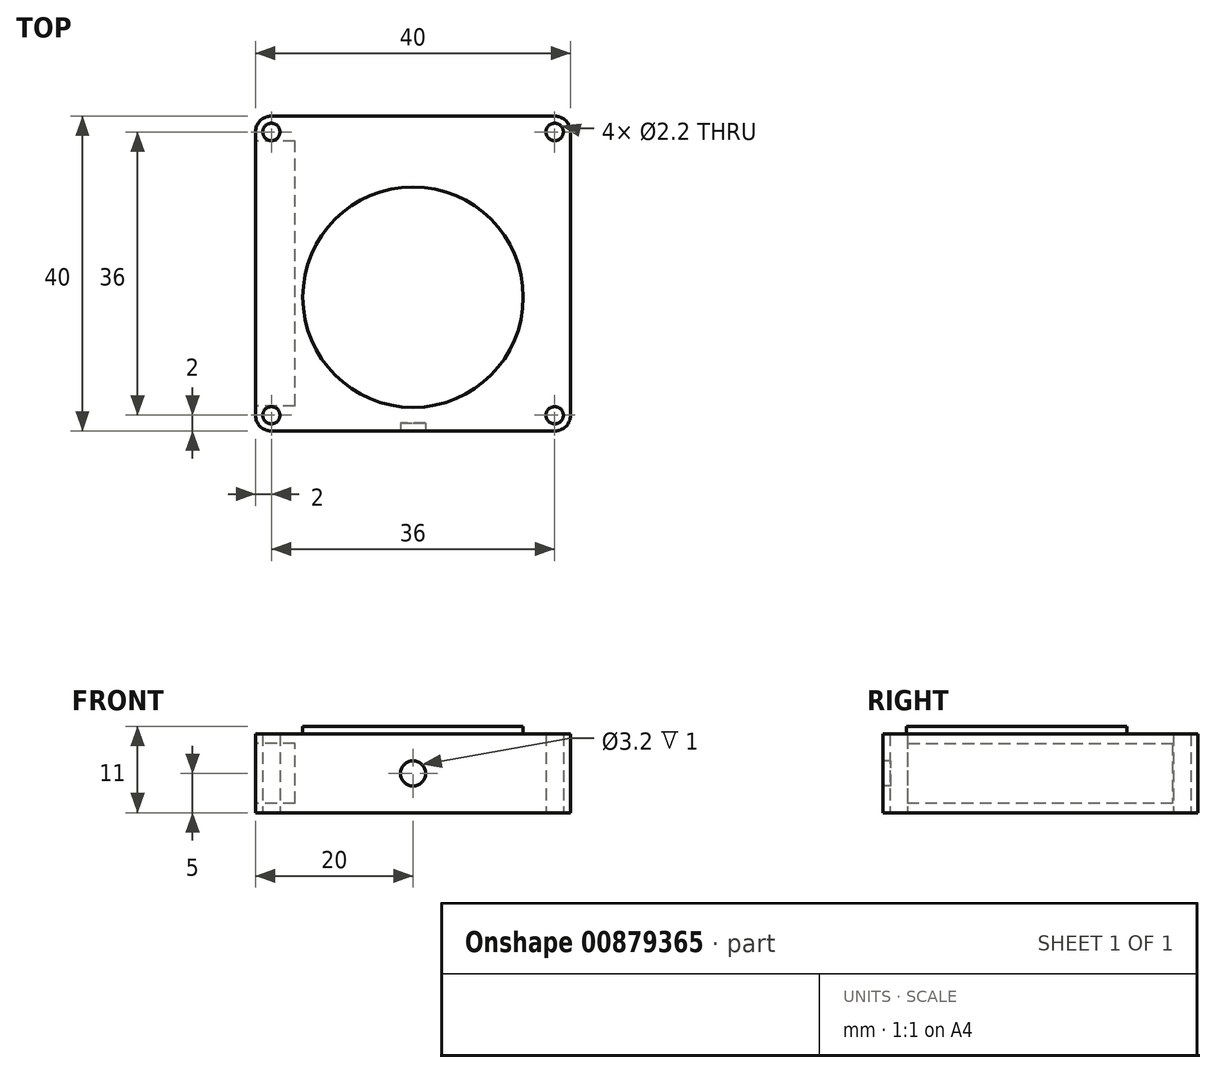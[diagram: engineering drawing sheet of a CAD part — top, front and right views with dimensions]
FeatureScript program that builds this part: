
annotation { "Feature Type Name" : "Feature", "Feature Type Description" : "" }
export const myFeature = defineFeature(function(context is Context, id is Id, definition is map)
    precondition{}
    {
        {
            var Q0;
            Q0=qCreatedBy(makeId("Top.planeOp"),FACE);
            var sketch = newSketch(context, id + "F0", { "sketchPlane" : qUnion([Q0])});
            skLineSegment(sketch, "E0.bottom", {"start": v(20, -20) * mm, "end": v(-20, -20) * mm});
            skLineSegment(sketch, "E0.top", {"start": v(20, 20) * mm, "end": v(-20, 20) * mm});
            skLineSegment(sketch, "E0.left", {"start": v(20, -20) * mm, "end": v(20, 20) * mm});
            skLineSegment(sketch, "E0.right", {"start": v(-20, -20) * mm, "end": v(-20, 20) * mm});
            skPoint(sketch, "E0.middle", {"position": v(0, 0) * mm});
            skPoint(sketch, "E1", {"position": v(-18, 18) * mm});
            skPoint(sketch, "E2", {"position": v(-18, -18) * mm});
            skPoint(sketch, "E3", {"position": v(18, 18) * mm});
            skPoint(sketch, "E4", {"position": v(18, -18) * mm});
            skSolve(sketch);
        }
        {
            var Q0;
            Q0=makeQuery(id+"F0.imprint","IMPRINT",FACE,{"disambiguationData":[TD([[makeQuery(id+"F0.imprint","IMPRINT",EDGE,{"derivedFrom":sQuery(id+"F0.wireOp",EDGE,"E0.bottom")}),-1.0]])]});
            extrude(context, id + "F1", {"entities" : qUnion([Q0]), "depth" : 10 * mm, "offsetDistance" : 25 * mm});
        }
        {
            var Q0;
            Q0=sQuery(id+"F0.wireOp",VERTEX,"E2");
            var Q1;
            Q1=sQuery(id+"F0.wireOp",VERTEX,"E1");
            var Q2;
            Q2=sQuery(id+"F0.wireOp",VERTEX,"E3");
            var Q3;
            Q3=sQuery(id+"F0.wireOp",VERTEX,"E4");
            var Q4;
            Q4=makeQuery(id+"F1.opExtrude","SWEPT_BODY",BODY,{"disambiguationData":[OSD([sQuery(id+"F0.wireOp",EDGE,"E0.bottom"),sQuery(id+"F0.wireOp",EDGE,"E0.top"),sQuery(id+"F0.wireOp",EDGE,"E0.left"),sQuery(id+"F0.wireOp",EDGE,"E0.right")])]});
            hole(context, id + "F2", {"style" : HoleStyle.SIMPLE, "endStyle" : HoleEndStyle.BLIND, "oppositeDirection" : true, "holeDiameter" : 2.2 * mm, "majorDiameter" : 5 * mm, "holeDepth" : 40 * mm, "isTappedThrough" : true, "tappedDepth" : 12 * mm, "tapClearance" : 3, "locations" : qUnion([Q0, Q1, Q2, Q3]), "scope" : qUnion([Q4])});
        }
        {
            var Q0;
            Q0=makeQuery(id+"F1.opExtrude","SWEPT_EDGE",EDGE,{"disambiguationData":[OSD([sQuery(id+"F0.wireOp",EDGE,"E0.bottom"),sQuery(id+"F0.wireOp",EDGE,"E0.right")])]});
            var Q1;
            Q1=makeQuery(id+"F1.opExtrude","SWEPT_EDGE",EDGE,{"disambiguationData":[OSD([sQuery(id+"F0.wireOp",EDGE,"E0.top"),sQuery(id+"F0.wireOp",EDGE,"E0.right")])]});
            var Q2;
            Q2=makeQuery(id+"F1.opExtrude","SWEPT_EDGE",EDGE,{"disambiguationData":[OSD([sQuery(id+"F0.wireOp",EDGE,"E0.bottom"),sQuery(id+"F0.wireOp",EDGE,"E0.left")])]});
            var Q3;
            Q3=makeQuery(id+"F1.opExtrude","SWEPT_EDGE",EDGE,{"disambiguationData":[OSD([sQuery(id+"F0.wireOp",EDGE,"E0.top"),sQuery(id+"F0.wireOp",EDGE,"E0.left")])]});
            fillet(context, id + "F3", {"entities" : qUnion([Q0, Q1, Q2, Q3]), "tangentPropagation" : true, "radius" : 2 * mm, "defaultsChanged" : false, "vertexSettings" : [], "allowEdgeOverflow" : false});
        }
        {
            var Q0;
            Q0=makeQuery(id+"F1.opExtrude","CAP_FACE",FACE,{"disambiguationData":[OSD([sQuery(id+"F0.wireOp",EDGE,"E0.bottom"),sQuery(id+"F0.wireOp",EDGE,"E0.top"),sQuery(id+"F0.wireOp",EDGE,"E0.left"),sQuery(id+"F0.wireOp",EDGE,"E0.right")])],"isStart":false});
            var sketch = newSketch(context, id + "F4", { "sketchPlane" : qUnion([Q0])});
            skCircle(sketch, "E5", {"center": v(0, -3) * mm, "radius": 14 * mm});
            skSolve(sketch);
        }
        {
            var Q0;
            Q0=makeQuery(id+"F4.imprint","IMPRINT",FACE,{"disambiguationData":[TD([[makeQuery(id+"F4.imprint","IMPRINT",EDGE,{"derivedFrom":sQuery(id+"F4.wireOp",EDGE,"E5")}),1.0]])]});
            extrude(context, id + "F5", {"entities" : qUnion([Q0]), "operationType" : NewBodyOperationType.ADD, "depth" : 1 * mm, "offsetDistance" : 25 * mm});
        }
        {
            var Q0;
            Q0=makeQuery(id+"F1.opExtrude","SWEPT_FACE",FACE,{"disambiguationData":[OSD([sQuery(id+"F0.wireOp",EDGE,"E0.right")])]});
            var sketch = newSketch(context, id + "F6", { "sketchPlane" : qUnion([Q0])});
            skLineSegment(sketch, "E6.0", {"start": v(16.8, 8.8) * mm, "end": v(-16.8, 8.8) * mm});
            skLineSegment(sketch, "E6.1", {"start": v(16.8, 1.2) * mm, "end": v(16.8, 8.8) * mm});
            skLineSegment(sketch, "E6.2", {"start": v(-16.8, 1.2) * mm, "end": v(16.8, 1.2) * mm});
            skLineSegment(sketch, "E6.3", {"start": v(-16.8, 8.8) * mm, "end": v(-16.8, 1.2) * mm});
            skSolve(sketch);
        }
        {
            var Q0;
            Q0=makeQuery(id+"F6.imprint","IMPRINT",FACE,{"disambiguationData":[TD([[makeQuery(id+"F6.imprint","IMPRINT",EDGE,{"derivedFrom":sQuery(id+"F6.wireOp",EDGE,"E6.0")}),1.0]])]});
            extrude(context, id + "F7", {"entities" : qUnion([Q0]), "operationType" : NewBodyOperationType.REMOVE, "oppositeDirection" : true, "depth" : 5 * mm, "offsetDistance" : 25 * mm});
        }
        {
            var Q0;
            Q0=makeQuery(id+"F1.opExtrude","SWEPT_FACE",FACE,{"disambiguationData":[OSD([sQuery(id+"F0.wireOp",EDGE,"E0.bottom")])]});
            var sketch = newSketch(context, id + "F8", { "sketchPlane" : qUnion([Q0])});
            skLineSegment(sketch, "E7.bottom", {"start": v(-10, 10) * mm, "end": v(-5.55, 10) * mm});
            skLineSegment(sketch, "E7.top", {"start": v(-10, 0) * mm, "end": v(-5.55, 0) * mm});
            skLineSegment(sketch, "E7.left", {"start": v(-10, 10) * mm, "end": v(-10, 0) * mm});
            skLineSegment(sketch, "E7.right", {"start": v(-5.55, 10) * mm, "end": v(-5.55, 0) * mm});
            skCircle(sketch, "E8", {"center": v(0, 5) * mm, "radius": 1.6 * mm});
            skPoint(sketch, "E8.centerSnap0", {"position": v(18, 5) * mm});
            skSolve(sketch);
        }
        {
            var Q0;
            Q0=makeQuery(id+"F8.imprint","IMPRINT",FACE,{"disambiguationData":[TD([[makeQuery(id+"F8.imprint","IMPRINT",EDGE,{"derivedFrom":sQuery(id+"F8.wireOp",EDGE,"E8")}),1.0]])]});
            extrude(context, id + "F9", {"entities" : qUnion([Q0]), "operationType" : NewBodyOperationType.REMOVE, "oppositeDirection" : true, "depth" : 1 * mm, "offsetDistance" : 25 * mm});
        }
    });
